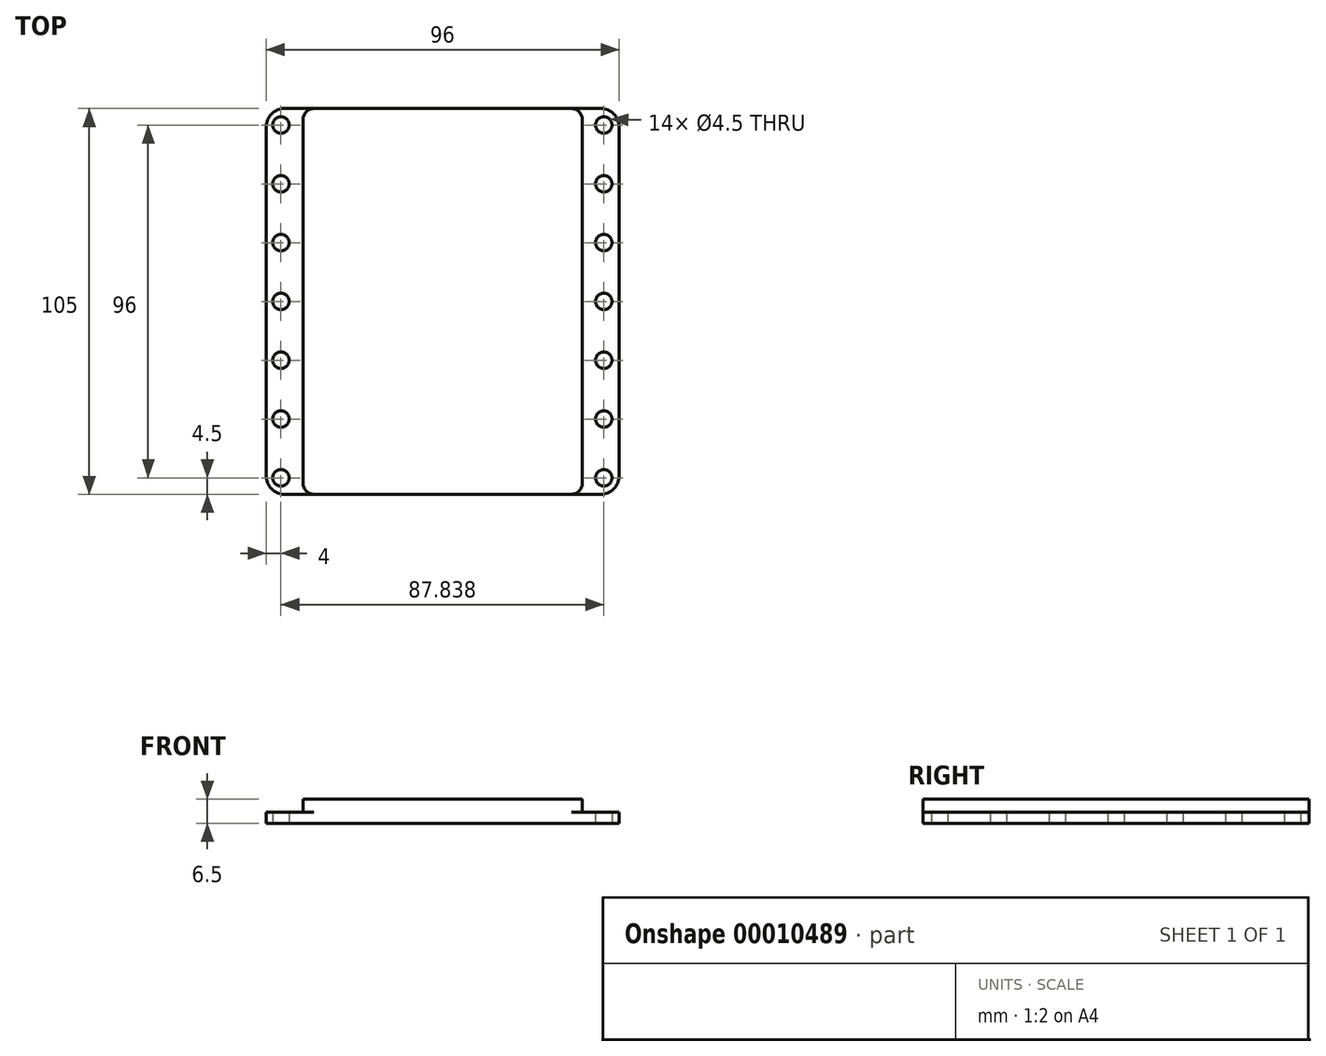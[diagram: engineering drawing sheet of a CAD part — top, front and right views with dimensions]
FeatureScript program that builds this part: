
annotation { "Feature Type Name" : "Feature", "Feature Type Description" : "" }
export const myFeature = defineFeature(function(context is Context, id is Id, definition is map)
    precondition{}
    {
        {
            var Q0;
            Q0=qCreatedBy(makeId("Front.planeOp"),FACE);
            var sketch = newSketch(context, id + "F0", { "sketchPlane" : qUnion([Q0])});
            skLineSegment(sketch, "E0.bottom", {"start": v(0, 0) * mm, "end": v(96, 0) * mm});
            skLineSegment(sketch, "E0.top", {"start": v(0, 3) * mm, "end": v(10, 3) * mm});
            skLineSegment(sketch, "E0.left", {"start": v(0, 0) * mm, "end": v(0, 3) * mm});
            skLineSegment(sketch, "E0.right", {"start": v(96, 0) * mm, "end": v(96, 3) * mm});
            skLineSegment(sketch, "E1.rect.bottom", {"start": v(86, 6.5) * mm, "end": v(10, 6.5) * mm});
            skLineSegment(sketch, "E1.rect.left", {"start": v(86, 6.5) * mm, "end": v(86, 3) * mm});
            skLineSegment(sketch, "E1.rect.right", {"start": v(10, 6.5) * mm, "end": v(10, 3) * mm});
            skPoint(sketch, "E1.rect.middle", {"position": v(48, 3) * mm});
            skLineSegment(sketch, "E2.trimOffspring", {"start": v(86, 3) * mm, "end": v(96, 3) * mm});
            skPoint(sketch, "E3.orphan", {"position": v(86, -0.5) * mm});
            skPoint(sketch, "E4.orphan", {"position": v(10, -0.5) * mm});
            skSolve(sketch);
        }
        {
            var Q0;
            Q0 = qSketchRegion(id + "F0", true);
            extrude(context, id + "F1", {"entities" : qUnion([Q0]), "depth" : 105 * mm});
        }
        {
            var Q0;
            Q0=makeQuery(id+"F1.opExtrude","CAP_EDGE",EDGE,{"disambiguationData":[OSD([sQuery(id+"F0.wireOp",EDGE,"E1.rect.left")])],"isStart":false});
            var Q1;
            Q1=makeQuery(id+"F1.opExtrude","CAP_EDGE",EDGE,{"disambiguationData":[OSD([sQuery(id+"F0.wireOp",EDGE,"E1.rect.left")])],"isStart":true});
            var Q2;
            Q2=makeQuery(id+"F1.opExtrude","CAP_EDGE",EDGE,{"disambiguationData":[OSD([sQuery(id+"F0.wireOp",EDGE,"E1.rect.right")])],"isStart":false});
            var Q3;
            Q3=makeQuery(id+"F1.opExtrude","CAP_EDGE",EDGE,{"disambiguationData":[OSD([sQuery(id+"F0.wireOp",EDGE,"E1.rect.right")])],"isStart":true});
            fillet(context, id + "F2", {"entities" : qUnion([Q0, Q1, Q2, Q3]), "radius" : 3 * mm, "tangentPropagation" : true, "allowEdgeOverflow" : false});
        }
        {
            var Q0;
            Q0=makeQuery(id+"F1.opExtrude","CAP_EDGE",EDGE,{"disambiguationData":[OSD([sQuery(id+"F0.wireOp",EDGE,"E0.left")])],"isStart":true});
            var Q1;
            Q1=makeQuery(id+"F1.opExtrude","CAP_EDGE",EDGE,{"disambiguationData":[OSD([sQuery(id+"F0.wireOp",EDGE,"E0.right")])],"isStart":true});
            var Q2;
            Q2=makeQuery(id+"F1.opExtrude","CAP_EDGE",EDGE,{"disambiguationData":[OSD([sQuery(id+"F0.wireOp",EDGE,"E0.right")])],"isStart":false});
            var Q3;
            Q3=makeQuery(id+"F1.opExtrude","CAP_EDGE",EDGE,{"disambiguationData":[OSD([sQuery(id+"F0.wireOp",EDGE,"E0.left")])],"isStart":false});
            fillet(context, id + "F3", {"entities" : qUnion([Q0, Q1, Q2, Q3]), "radius" : 5 * mm, "tangentPropagation" : true, "allowEdgeOverflow" : false});
        }
        {
            var Q0;
            Q0=makeQuery(id+"F1.opExtrude","SWEPT_FACE",FACE,{"disambiguationData":[OSD([sQuery(id+"F0.wireOp",EDGE,"E0.bottom")])]});
            var sketch = newSketch(context, id + "F4", { "sketchPlane" : qUnion([Q0])});
            skLineSegment(sketch, "E5", {"start": v(48, 105) * mm, "end": v(48, 0) * mm, "construction": true});
            skCircle(sketch, "E6", {"center": v(4, 100.5) * mm, "radius": 2.25 * mm});
            skCircle(sketch, "E7.0.1.0", {"center": v(4, 84.5) * mm, "radius": 2.25 * mm});
            skCircle(sketch, "E7.0.2.0", {"center": v(4, 68.5) * mm, "radius": 2.25 * mm});
            skCircle(sketch, "E7.0.3.0", {"center": v(4, 52.5) * mm, "radius": 2.25 * mm});
            skCircle(sketch, "E7.0.4.0", {"center": v(4, 36.5) * mm, "radius": 2.25 * mm});
            skCircle(sketch, "E7.0.5.0", {"center": v(4, 20.5) * mm, "radius": 2.25 * mm});
            skCircle(sketch, "E7.0.6.0", {"center": v(4, 4.5) * mm, "radius": 2.25 * mm});
            skCircle(sketch, "E7.1.0.0", {"center": v(91.84, 100.5) * mm, "radius": 2.25 * mm});
            skCircle(sketch, "E7.1.1.0", {"center": v(91.84, 84.5) * mm, "radius": 2.25 * mm});
            skCircle(sketch, "E7.1.2.0", {"center": v(91.84, 68.5) * mm, "radius": 2.25 * mm});
            skCircle(sketch, "E7.1.3.0", {"center": v(91.84, 52.5) * mm, "radius": 2.25 * mm});
            skCircle(sketch, "E7.1.4.0", {"center": v(91.84, 36.5) * mm, "radius": 2.25 * mm});
            skCircle(sketch, "E7.1.5.0", {"center": v(91.84, 20.5) * mm, "radius": 2.25 * mm});
            skCircle(sketch, "E7.1.6.0", {"center": v(91.84, 4.5) * mm, "radius": 2.25 * mm});
            skLineSegment(sketch, "E7.direction1", {"start": v(4, 100.5) * mm, "end": v(91.84, 100.5) * mm, "construction": true});
            skLineSegment(sketch, "E7.direction2", {"start": v(4, 100.5) * mm, "end": v(4, 84.5) * mm, "construction": true});
            skSolve(sketch);
        }
        {
            var Q0;
            Q0 = qSketchRegion(id + "F4", true);
            extrude(context, id + "F5", {"entities" : qUnion([Q0]), "operationType" : NewBodyOperationType.REMOVE, "endBound" : BoundingType.UP_TO_NEXT, "oppositeDirection" : true, "depth" : 25 * mm});
        }
    });
